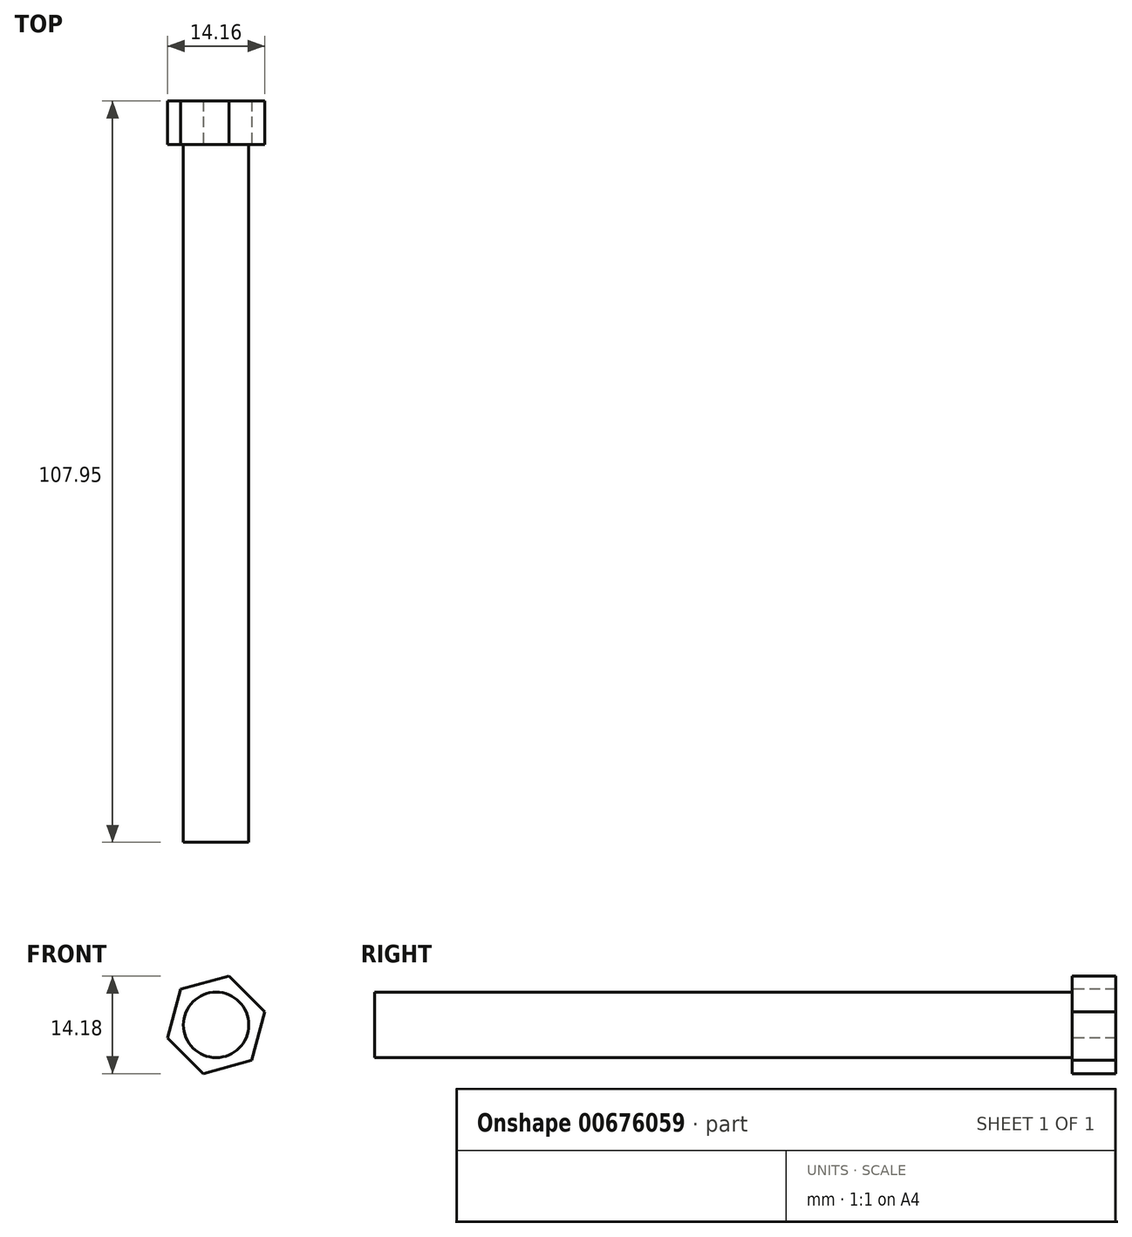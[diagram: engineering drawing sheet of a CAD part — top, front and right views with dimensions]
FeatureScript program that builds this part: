
annotation { "Feature Type Name" : "Feature", "Feature Type Description" : "" }
export const myFeature = defineFeature(function(context is Context, id is Id, definition is map)
    precondition{}
    {
        {
            var Q0;
            Q0=qCreatedBy(makeId("Front.planeOp"),FACE);
            var sketch = newSketch(context, id + "F0", { "sketchPlane" : qUnion([Q0])});
            skCircle(sketch, "E0", {"center": v(0, 0) * mm, "radius": 4.76 * mm});
            skSolve(sketch);
        }
        {
            var Q0;
            Q0 = qSketchRegion(id + "F0", true);
            extrude(context, id + "F1", {"entities" : qUnion([Q0]), "depth" : 101.6 * mm, "offsetDistance" : 25.4 * mm});
        }
        {
            var Q0;
            Q0=qCreatedBy(makeId("Front.planeOp"),FACE);
            var sketch = newSketch(context, id + "F2", { "sketchPlane" : qUnion([Q0])});
            skCircle(sketch, "E1.cCircle", {"center": v(0, 0) * mm, "radius": 6.35 * mm, "construction": true});
            skLineSegment(sketch, "E1.0", {"start": v(7.08, 1.9) * mm, "end": v(5.2, -5.18) * mm});
            skLineSegment(sketch, "E1.1", {"start": v(5.2, -5.18) * mm, "end": v(-1.89, -7.09) * mm});
            skLineSegment(sketch, "E1.2", {"start": v(-1.89, -7.09) * mm, "end": v(-7.08, -1.9) * mm});
            skLineSegment(sketch, "E1.3", {"start": v(-7.08, -1.9) * mm, "end": v(-5.2, 5.18) * mm});
            skLineSegment(sketch, "E1.4", {"start": v(-5.2, 5.18) * mm, "end": v(1.89, 7.09) * mm});
            skLineSegment(sketch, "E1.5", {"start": v(1.89, 7.09) * mm, "end": v(7.08, 1.9) * mm});
            skPoint(sketch, "E1.0.midPoint", {"position": v(6.14, -1.63) * mm});
            skSolve(sketch);
        }
        {
            var Q0;
            Q0=makeQuery(id+"F2.imprint","IMPRINT",FACE,{"disambiguationData":[TD([[makeQuery(id+"F2.imprint","IMPRINT",EDGE,{"derivedFrom":sQuery(id+"F2.wireOp",EDGE,"E1.0")}),-1.0]])]});
            extrude(context, id + "F3", {"entities" : qUnion([Q0]), "operationType" : NewBodyOperationType.ADD, "oppositeDirection" : true, "depth" : 6.35 * mm, "offsetDistance" : 25.4 * mm});
        }
    });
